# Revit family: PUHY-EP1100YSNW-A
name_source: partatom
category: Mechanical Equipment
revit_build: Autodesk Revit Architecture 2012 (Build: 20110916_2132(x64)
units: mm (PartAtom-declared; Revit-internal decimal feet)

## types (6) — shared parameters
Airflow Rate (m3/h) = 48600
Airflow Rate (m3/min) = 810
Compressor Motor Output (kW) = 30.5
Compressor_Lubricant = MEL32
Compressor_Quantity = 3
Compressor_Type = Inverter scroll hermetic compressor
Cooling Capacity (kW) = 124
Cooling EER (kW/kW) = 4.34
Cooling Power Input (kW) = 28.56
Depth = 740 mm  [stored 2.42782 ft]
External Finish = Pre-coated galvanized steel sheets (+powder coating for -BS type) <MUNSELL 5Y 8/1 or similar>
Fan Motor Output (kW) = 2.76
Fan_Quantity = 6
Fan_Type = Propeller Fan
Gas pipe_radius = 21 mm
Heating COP (kW/kW) = 4.24
Heating Capacity (kW) = 140
Heating Power Input (kW) = 33
Height = 1858 mm  [stored 6.0958 ft]
Indoor Unit Model/Quantity = P15 to P250/3 to 50
Indoor Unit Total Capacity = 50 to 130% of outdoor unit capacity
Liquid pipe_radius = 10 mm  [stored 0.0328084 ft]
Manufacturer = Mitsubishi Electric Corporation
Maximum Circuit Ampacity (A) = 76.4
Model = PUHY-EP1100YSNW-A
Note_1 = Refrigerant pipe diameters may change depending on the installation condition. Please refer to the installation manual.
Outdoor unit 1 = PUHY-EP400YNW-A
Outdoor unit 2 = PUHY-EP350YNW-A
Outdoor unit 3 = PUHY-EP350YNW-A
Phase = 3
Protection Devices_High pressure (MPa) = High pressure sensor, High pressure switch at 4.15
Protection Devices_Inverter circuit (COMP./FAN) = Over-heat protection, Over-current protection
Refrigerant Charge (kg) = 30.4
Refrigerant type = R410A
Sound Pressure Level (dB(A)) Cooling mode = 68.5
Sound Pressure Level (dB(A)) Heating mode = 69
Space View = Yes
Subcategory = HVAC
Temp. range of heating (Indoor temp.) (D.B.) = 15.0 to 27.0
Temp. range of heating (Outdoor temp.) (W.B.) = -20.0 to 15.5
URL = http://www.mitsubishielectric.com
Unit Weight (kg) = 875
Width = 3780 mm  [stored 12.4016 ft]
zero-valued in all types: Equip_No., External static pressure (Pa), SerialNumber, TagNumber

## per-type parameters (varying)
| type | Cooling Current (A) | Heating Current (A) | Hertz | Voltage |
| PUHY-EP1100YSNW-A_380V_50Hz | 48.2 | 55.7 | 50 Hz | 380 V |
| PUHY-EP1100YSNW-A_380V_60Hz | 48.2 | 55.7 | 60 Hz | 380 V |
| PUHY-EP1100YSNW-A_400V_50Hz | 45.8 | 52.9 | 50 Hz | 400 V |
| PUHY-EP1100YSNW-A_400V_60Hz | 45.8 | 52.9 | 60 Hz | 400 V |
| PUHY-EP1100YSNW-A_415V_50Hz | 44.1 | 51 | 50 Hz | 415 V |
| PUHY-EP1100YSNW-A_415V_60Hz | 44.1 | 51 | 60 Hz | 415 V |

note: [stored X ft] marks values corroborated as IEEE doubles in the binary element streams (Revit-internal decimal feet)

## geometry (parser evidence)
native form markers: Blend x20, Sweep x8
no freeform markers — native parametric forms only
